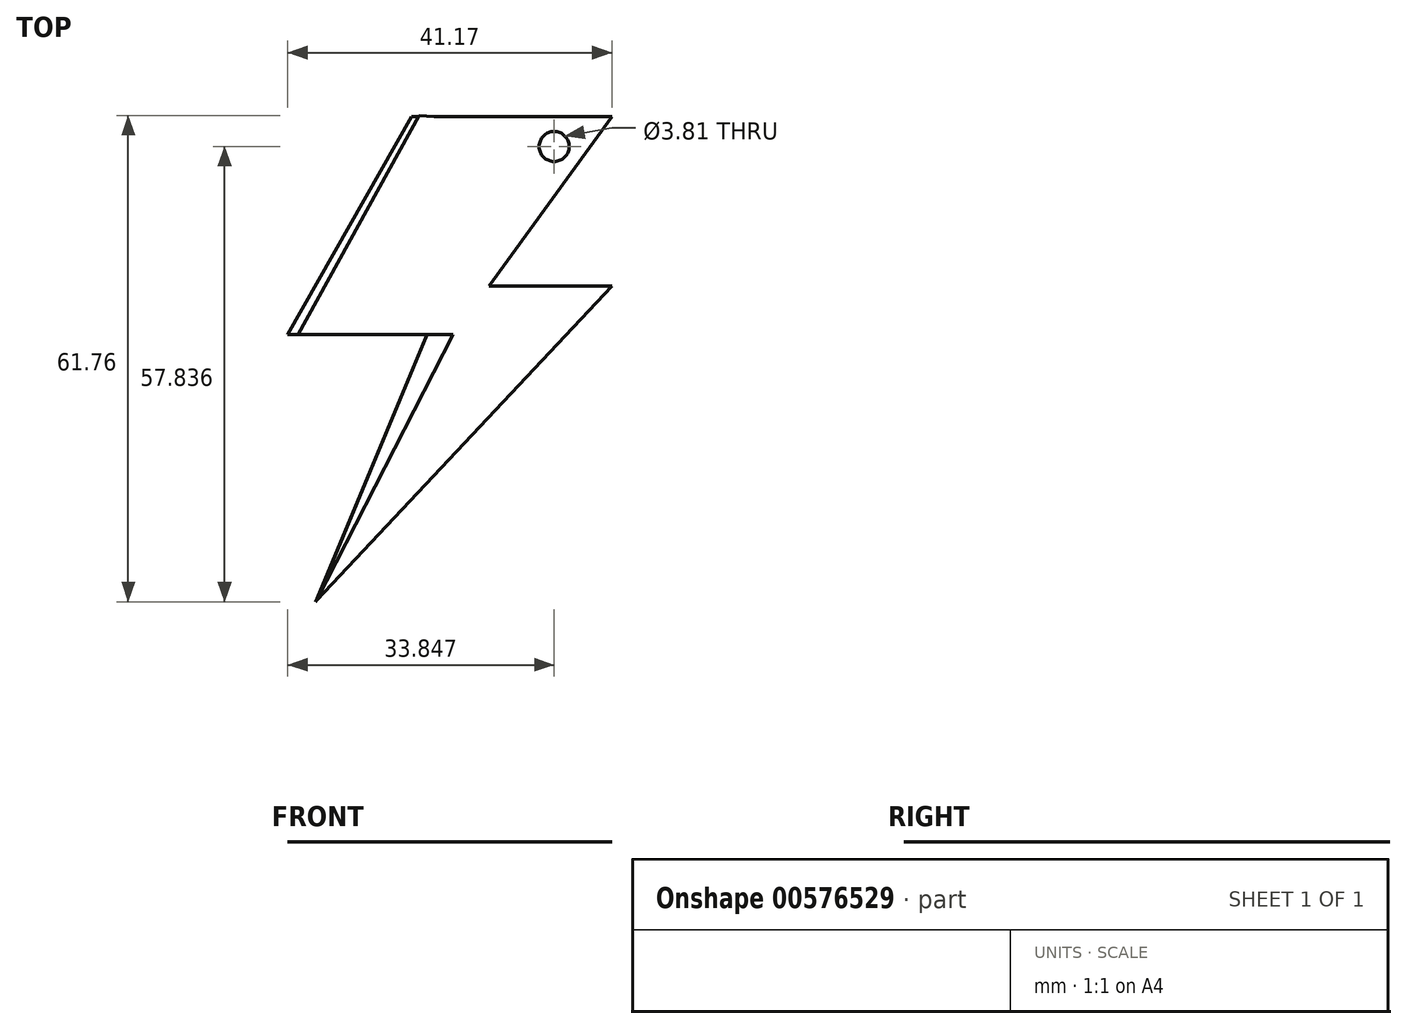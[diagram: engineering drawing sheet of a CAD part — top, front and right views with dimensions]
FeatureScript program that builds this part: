
annotation { "Feature Type Name" : "Feature", "Feature Type Description" : "" }
export const myFeature = defineFeature(function(context is Context, id is Id, definition is map)
    precondition{}
    {
        {
            var Q0;
            Q0=qCreatedBy(makeId("Top.planeOp"),FACE);
            var sketch = newSketch(context, id + "F0", { "sketchPlane" : qUnion([Q0])});
            skLineSegment(sketch, "E0", {"start": v(15.58, 6.17) * mm, "end": v(0, 6.17) * mm});
            skLineSegment(sketch, "E1", {"start": v(0, 6.17) * mm, "end": v(15.58, 27.69) * mm});
            skLineSegment(sketch, "E2", {"start": v(15.58, 27.69) * mm, "end": v(-9.85, 27.69) * mm});
            skLineSegment(sketch, "E3", {"start": v(-9.85, 27.69) * mm, "end": v(-25.6, 0) * mm});
            skLineSegment(sketch, "E4", {"start": v(15.58, 6.17) * mm, "end": v(-22.08, -33.93) * mm});
            skLineSegment(sketch, "E5", {"start": v(-22.08, -33.93) * mm, "end": v(-7.9, 0) * mm});
            skLineSegment(sketch, "E6", {"start": v(-7.9, 0) * mm, "end": v(-25.6, 0) * mm});
            skSolve(sketch);
        }
        {
            var Q0;
            Q0=makeQuery(id+"F0.imprint","IMPRINT",FACE,{"disambiguationData":[TD([[makeQuery(id+"F0.imprint","IMPRINT",EDGE,{"derivedFrom":sQuery(id+"F0.wireOp",EDGE,"E0")}),1.0]])]});
            extrude(context, id + "F1", {"entities" : qUnion([Q0]), "depth" : 1 / 406.4 * mm, "offsetDistance" : 25.4 * mm});
        }
        {
            var Q0;
            Q0=makeQuery(id+"F1.opExtrude","CAP_FACE",FACE,{"disambiguationData":[OSD([sQuery(id+"F0.wireOp",EDGE,"E0"),sQuery(id+"F0.wireOp",EDGE,"E1"),sQuery(id+"F0.wireOp",EDGE,"E2"),sQuery(id+"F0.wireOp",EDGE,"E3"),sQuery(id+"F0.wireOp",EDGE,"E4"),sQuery(id+"F0.wireOp",EDGE,"E5"),sQuery(id+"F0.wireOp",EDGE,"E6")])],"isStart":false});
            cPlane(context, id + "F2", {"entities" : qUnion([Q0]), "cplaneType" : CPlaneType.OFFSET, "offset" : 0 * mm, "width" : 152.4 * mm, "height" : 152.4 * mm});
        }
        {
            var Q0;
            Q0=qCreatedBy(id+"F2.planeOp",FACE);
            var sketch = newSketch(context, id + "F3", { "sketchPlane" : qUnion([Q0])});
            skLineSegment(sketch, "E7", {"start": v(-8.88, 27.83) * mm, "end": v(-24.24, 0) * mm});
            skLineSegment(sketch, "E8", {"start": v(-24.24, 0) * mm, "end": v(-21.93, 0) * mm});
            skLineSegment(sketch, "E9", {"start": v(-21.93, 0) * mm, "end": v(-6.97, 27.7) * mm});
            skLineSegment(sketch, "E10", {"start": v(-6.97, 27.7) * mm, "end": v(-8.88, 27.83) * mm});
            skSolve(sketch);
        }
        {
            var Q0;
            Q0=makeQuery(id+"F3.imprint","IMPRINT",FACE,{"disambiguationData":[TD([[makeQuery(id+"F3.imprint","IMPRINT",EDGE,{"derivedFrom":sQuery(id+"F3.wireOp",EDGE,"E7")}),1.0]])]});
            extrude(context, id + "F4", {"entities" : qUnion([Q0]), "operationType" : NewBodyOperationType.ADD, "depth" : 1 / 1270 * mm, "offsetDistance" : 25.4 * mm});
        }
        {
            var Q0;
            {var subQ0=sQuery(id+"F0.wireOp",EDGE,"E4");var subQ4=sQuery(id+"F0.wireOp",EDGE,"E2");var subQ5=sQuery(id+"F0.wireOp",EDGE,"E1");var subQ6=sQuery(id+"F0.wireOp",EDGE,"E0");var subQ7=sQuery(id+"F0.wireOp",EDGE,"E5");var subQ8=sQuery(id+"F0.wireOp",EDGE,"E6");Q0=makeQuery(id+"F4.boolean.opBoolean","SPLIT",FACE,{"disambiguationData":[TD([makeQuery(id+"F1.opExtrude","SWEPT_FACE",FACE,{"disambiguationData":[OSD([subQ6])]})])],"derivedFrom":makeQuery(id+"F1.opExtrude","CAP_FACE",FACE,{"disambiguationData":[OSD([subQ6,subQ5,subQ4,sQuery(id+"F0.wireOp",EDGE,"E3"),subQ0,subQ7,subQ8])],"isStart":false})});}
            var sketch = newSketch(context, id + "F5", { "sketchPlane" : qUnion([Q0])});
            skLineSegment(sketch, "E11", {"start": v(-7.9, 0) * mm, "end": v(-4.56, 0) * mm});
            skLineSegment(sketch, "E12", {"start": v(-4.56, 0) * mm, "end": v(-21.93, -33.77) * mm});
            skLineSegment(sketch, "E13", {"start": v(-21.93, -33.77) * mm, "end": v(-7.9, 0) * mm});
            skSolve(sketch);
        }
        {
            var Q0;
            Q0=makeQuery(id+"F5.imprint","IMPRINT",FACE,{"disambiguationData":[TD([[makeQuery(id+"F5.imprint","IMPRINT",EDGE,{"derivedFrom":sQuery(id+"F5.wireOp",EDGE,"E11")}),-1.0]])]});
            extrude(context, id + "F6", {"entities" : qUnion([Q0]), "operationType" : NewBodyOperationType.ADD, "depth" : 1 / 1270 * mm, "offsetDistance" : 25.4 * mm});
        }
        {
            var Q0;
            {var subQ0=sQuery(id+"F3.wireOp",EDGE,"E9");var subQ1=makeQuery(id+"F4.opExtrude","SWEPT_FACE",FACE,{"disambiguationData":[OSD([subQ0])]});var subQ2=sQuery(id+"F3.wireOp",EDGE,"E8");var subQ3=makeQuery(id+"F4.opExtrude","SWEPT_FACE",FACE,{"disambiguationData":[OSD([subQ2])]});var subQ4=sQuery(id+"F0.wireOp",EDGE,"E6");var subQ5=makeQuery(id+"F1.opExtrude","SWEPT_FACE",FACE,{"disambiguationData":[OSD([subQ4])]});var subQ6=sQuery(id+"F0.wireOp",EDGE,"E5");var subQ7=makeQuery(id+"F1.opExtrude","SWEPT_FACE",FACE,{"disambiguationData":[OSD([subQ6])]});var subQ8=sQuery(id+"F3.wireOp",EDGE,"E10");var subQ9=makeQuery(id+"F4.opExtrude","CAP_FACE",FACE,{"disambiguationData":[OSD([sQuery(id+"F3.wireOp",EDGE,"E7"),subQ2,subQ0,subQ8])],"isStart":true});var subQ10=sQuery(id+"F0.wireOp",EDGE,"E4");var subQ11=makeQuery(id+"F1.opExtrude","SWEPT_FACE",FACE,{"disambiguationData":[OSD([subQ10])]});var subQ12=sQuery(id+"F0.wireOp",EDGE,"E0");var subQ13=makeQuery(id+"F1.opExtrude","SWEPT_FACE",FACE,{"disambiguationData":[OSD([subQ12])]});var subQ14=sQuery(id+"F0.wireOp",EDGE,"E2");var subQ15=sQuery(id+"F0.wireOp",EDGE,"E1");var subQ16=makeQuery(id+"F1.opExtrude","CAP_FACE",FACE,{"disambiguationData":[OSD([subQ12,subQ15,subQ14,sQuery(id+"F0.wireOp",EDGE,"E3"),subQ10,subQ6,subQ4])],"isStart":false});var subQ17=makeQuery(id+"F1.opExtrude","SWEPT_FACE",FACE,{"disambiguationData":[OSD([subQ15])]});var subQ18=makeQuery(id+"F1.opExtrude","SWEPT_FACE",FACE,{"disambiguationData":[OSD([subQ14])]});var subQ19=makeQuery(id+"F4.opExtrude","SWEPT_FACE",FACE,{"disambiguationData":[OSD([subQ8])]});Q0=makeQuery(id+"F6.boolean.opBoolean","SPLIT",FACE,{"disambiguationData":[TD([subQ13,subQ16,subQ17,subQ18,subQ11,subQ7,subQ5,subQ9,subQ3,subQ1,subQ19,makeQuery(id+"F6.opExtrude","SWEPT_FACE",FACE,{"disambiguationData":[OSD([sQuery(id+"F5.wireOp",EDGE,"E11")])]}),makeQuery(id+"F6.opExtrude","SWEPT_FACE",FACE,{"disambiguationData":[OSD([sQuery(id+"F5.wireOp",EDGE,"E12")])]}),makeQuery(id+"F6.opExtrude","SWEPT_FACE",FACE,{"disambiguationData":[OSD([sQuery(id+"F5.wireOp",EDGE,"E13")])]})])],"derivedFrom":makeQuery(id+"F4.boolean.opBoolean","SPLIT",FACE,{"disambiguationData":[TD([subQ13])],"derivedFrom":subQ16})});}
            var sketch = newSketch(context, id + "F7", { "sketchPlane" : qUnion([Q0])});
            skPoint(sketch, "E14", {"position": v(8.26, 23.9) * mm});
            skSolve(sketch);
        }
        {
            var Q0;
            Q0=sQuery(id+"F7.wireOp",VERTEX,"E14");
            var Q1;
            Q1=makeQuery(id+"F1.opExtrude","SWEPT_BODY",BODY,{"disambiguationData":[OSD([sQuery(id+"F0.wireOp",EDGE,"E0"),sQuery(id+"F0.wireOp",EDGE,"E1"),sQuery(id+"F0.wireOp",EDGE,"E2"),sQuery(id+"F0.wireOp",EDGE,"E3"),sQuery(id+"F0.wireOp",EDGE,"E4"),sQuery(id+"F0.wireOp",EDGE,"E5"),sQuery(id+"F0.wireOp",EDGE,"E6")])]});
            hole(context, id + "F8", {"style" : HoleStyle.SIMPLE, "endStyle" : HoleEndStyle.THROUGH, "holeDiameter" : 3.8 * mm, "isTappedThrough" : true, "tappedDepth" : 12.7 * mm, "tapClearance" : 3, "locations" : qUnion([Q0]), "scope" : qUnion([Q1])});
        }
    });
